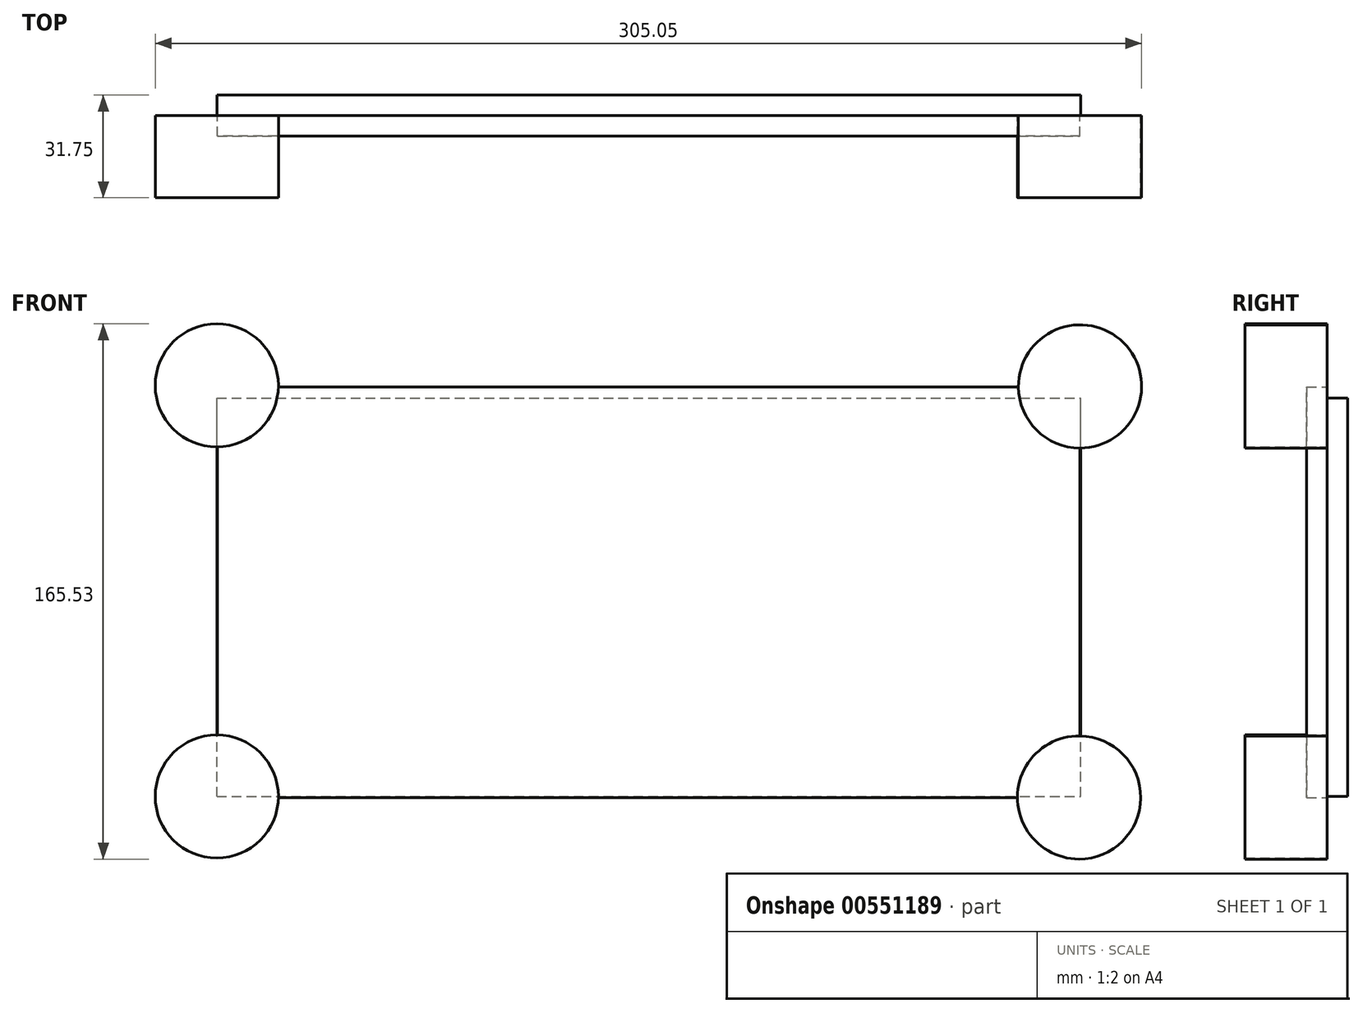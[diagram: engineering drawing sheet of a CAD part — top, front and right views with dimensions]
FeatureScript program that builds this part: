
annotation { "Feature Type Name" : "Feature", "Feature Type Description" : "" }
export const myFeature = defineFeature(function(context is Context, id is Id, definition is map)
    precondition{}
    {
        {
            var Q0;
            Q0=qCreatedBy(makeId("Front.planeOp"),FACE);
            var sketch = newSketch(context, id + "F0", { "sketchPlane" : qUnion([Q0])});
            skLineSegment(sketch, "E0.bottom", {"start": v(133.35, -63.5) * mm, "end": v(-133.35, -63.5) * mm});
            skLineSegment(sketch, "E0.top", {"start": v(133.35, 63.5) * mm, "end": v(-133.35, 63.5) * mm});
            skLineSegment(sketch, "E0.left", {"start": v(133.35, -63.5) * mm, "end": v(133.35, 63.5) * mm});
            skLineSegment(sketch, "E0.right", {"start": v(-133.35, -63.5) * mm, "end": v(-133.35, 63.5) * mm});
            skPoint(sketch, "E0.middle", {"position": v(0, 0) * mm});
            skLineSegment(sketch, "E1.bottom", {"start": v(114.3, -50.8) * mm, "end": v(-114.3, -50.8) * mm});
            skLineSegment(sketch, "E1.top", {"start": v(114.3, 50.8) * mm, "end": v(-114.3, 50.8) * mm});
            skLineSegment(sketch, "E1.left", {"start": v(114.3, -50.8) * mm, "end": v(114.3, 50.8) * mm});
            skLineSegment(sketch, "E1.right", {"start": v(-114.3, -50.8) * mm, "end": v(-114.3, 50.8) * mm});
            skLineSegment(sketch, "E2", {"start": v(-114.3, 25.4) * mm, "end": v(114.3, 25.4) * mm});
            skLineSegment(sketch, "E3", {"start": v(-114.3, 12.7) * mm, "end": v(114.3, 12.7) * mm});
            skLineSegment(sketch, "E4", {"start": v(-114.3, 0) * mm, "end": v(114.3, 0) * mm});
            skLineSegment(sketch, "E5", {"start": v(-114.3, -25.4) * mm, "end": v(114.3, -25.4) * mm});
            skLineSegment(sketch, "E6", {"start": v(-114.3, -38.1) * mm, "end": v(114.3, -38.1) * mm});
            skLineSegment(sketch, "E7", {"start": v(-114.3, 38.1) * mm, "end": v(114.3, 38.1) * mm});
            skLineSegment(sketch, "E8", {"start": v(114.3, -12.7) * mm, "end": v(-114.3, -12.7) * mm});
            skSolve(sketch);
        }
        {
            var Q0;
            Q0=makeQuery(id+"F0.imprint","IMPRINT",FACE,{"disambiguationData":[TD([[makeQuery(id+"F0.imprint","IMPRINT",EDGE,{"derivedFrom":sQuery(id+"F0.wireOp",EDGE,"E0.bottom")}),-1.0]])]});
            var sketch = newSketch(context, id + "F1", { "sketchPlane" : qUnion([Q0])});
            skCircle(sketch, "E9", {"center": v(-133.56, 63.97) * mm, "radius": 19.05 * mm});
            skCircle(sketch, "E10", {"center": v(133.39, 63.66) * mm, "radius": 19.05 * mm});
            skCircle(sketch, "E11", {"center": v(133.08, -63.46) * mm, "radius": 19.05 * mm});
            skCircle(sketch, "E12", {"center": v(-133.56, -63.15) * mm, "radius": 19.05 * mm});
            skSolve(sketch);
        }
        {
            var Q0;
            Q0 = qSketchRegion(id + "F0", true);
            var Q1;
            {var subQ0=sQuery(id+"F0.wireOp",EDGE,"E1.bottom");Q1=makeQuery(id+"F0.imprint","IMPRINT",FACE,{"disambiguationData":[TD([[makeQuery(id+"F0.imprint","IMPRINT",EDGE,{"derivedFrom":subQ0}),-1.0]])]});}
            var Q2;
            {var subQ0=sQuery(id+"F0.wireOp",EDGE,"E5");Q2=makeQuery(id+"F0.imprint","IMPRINT",FACE,{"disambiguationData":[TD([[makeQuery(id+"F0.imprint","IMPRINT",EDGE,{"derivedFrom":subQ0}),-1.0]])]});}
            var Q3;
            {var subQ0=sQuery(id+"F0.wireOp",EDGE,"E5");Q3=makeQuery(id+"F0.imprint","IMPRINT",FACE,{"disambiguationData":[TD([[makeQuery(id+"F0.imprint","IMPRINT",EDGE,{"derivedFrom":subQ0}),1.0]])]});}
            var Q4;
            {var subQ0=sQuery(id+"F0.wireOp",EDGE,"E4");Q4=makeQuery(id+"F0.imprint","IMPRINT",FACE,{"disambiguationData":[TD([[makeQuery(id+"F0.imprint","IMPRINT",EDGE,{"derivedFrom":subQ0}),-1.0]])]});}
            var Q5;
            {var subQ0=sQuery(id+"F0.wireOp",EDGE,"E3");Q5=makeQuery(id+"F0.imprint","IMPRINT",FACE,{"disambiguationData":[TD([[makeQuery(id+"F0.imprint","IMPRINT",EDGE,{"derivedFrom":subQ0}),-1.0]])]});}
            var Q6;
            {var subQ0=sQuery(id+"F0.wireOp",EDGE,"E2");Q6=makeQuery(id+"F0.imprint","IMPRINT",FACE,{"disambiguationData":[TD([[makeQuery(id+"F0.imprint","IMPRINT",EDGE,{"derivedFrom":subQ0}),-1.0]])]});}
            var Q7;
            {var subQ0=sQuery(id+"F0.wireOp",EDGE,"E2");Q7=makeQuery(id+"F0.imprint","IMPRINT",FACE,{"disambiguationData":[TD([[makeQuery(id+"F0.imprint","IMPRINT",EDGE,{"derivedFrom":subQ0}),1.0]])]});}
            var Q8;
            {var subQ0=sQuery(id+"F0.wireOp",EDGE,"E1.top");Q8=makeQuery(id+"F0.imprint","IMPRINT",FACE,{"disambiguationData":[TD([[makeQuery(id+"F0.imprint","IMPRINT",EDGE,{"derivedFrom":subQ0}),1.0]])]});}
            extrude(context, id + "F2", {"entities" : qUnion([Q0, Q1, Q2, Q3, Q4, Q5, Q6, Q7, Q8]), "depth" : 6.35 * mm, "offsetDistance" : 25.4 * mm});
        }
        {
            var Q0;
            Q0 = qSketchRegion(id + "F1", true);
            extrude(context, id + "F3", {"entities" : qUnion([Q0]), "operationType" : NewBodyOperationType.ADD, "depth" : 25.4 * mm, "offsetDistance" : 25.4 * mm});
        }
        {
            var Q0;
            Q0=makeQuery(id+"F3.boolean.opBoolean","MERGE",FACE,{"derivedFrom":[makeQuery(id+"F2.opExtrude","CAP_FACE",FACE,{"disambiguationData":[OSD([sQuery(id+"F0.wireOp",EDGE,"E0.bottom"),sQuery(id+"F0.wireOp",EDGE,"E0.top"),sQuery(id+"F0.wireOp",EDGE,"E0.left"),sQuery(id+"F0.wireOp",EDGE,"E0.right")])],"isStart":true}),makeQuery(id+"F3.opExtrude","CAP_FACE",FACE,{"disambiguationData":[OSD([sQuery(id+"F1.wireOp",EDGE,"E9")])],"isStart":true}),makeQuery(id+"F3.opExtrude","CAP_FACE",FACE,{"disambiguationData":[OSD([sQuery(id+"F1.wireOp",EDGE,"E10")])],"isStart":true}),makeQuery(id+"F3.opExtrude","CAP_FACE",FACE,{"disambiguationData":[OSD([sQuery(id+"F1.wireOp",EDGE,"E11")])],"isStart":true}),makeQuery(id+"F3.opExtrude","CAP_FACE",FACE,{"disambiguationData":[OSD([sQuery(id+"F1.wireOp",EDGE,"E12")])],"isStart":true})]});
            var sketch = newSketch(context, id + "F4", { "sketchPlane" : qUnion([Q0])});
            skLineSegment(sketch, "E13.bottom", {"start": v(133.56, -63.15) * mm, "end": v(-133.56, -63.15) * mm});
            skLineSegment(sketch, "E13.top", {"start": v(133.56, 60.06) * mm, "end": v(-133.56, 60.06) * mm});
            skLineSegment(sketch, "E13.left", {"start": v(133.56, -63.15) * mm, "end": v(133.56, 60.06) * mm});
            skLineSegment(sketch, "E13.right", {"start": v(-133.56, -63.15) * mm, "end": v(-133.56, 60.06) * mm});
            skPoint(sketch, "E13.middle", {"position": v(0, -1.55) * mm});
            skSolve(sketch);
        }
        {
            var Q0;
            Q0 = qSketchRegion(id + "F4", true);
            extrude(context, id + "F5", {"entities" : qUnion([Q0]), "operationType" : NewBodyOperationType.ADD, "depth" : 6.35 * mm, "offsetDistance" : 25.4 * mm});
        }
    });
